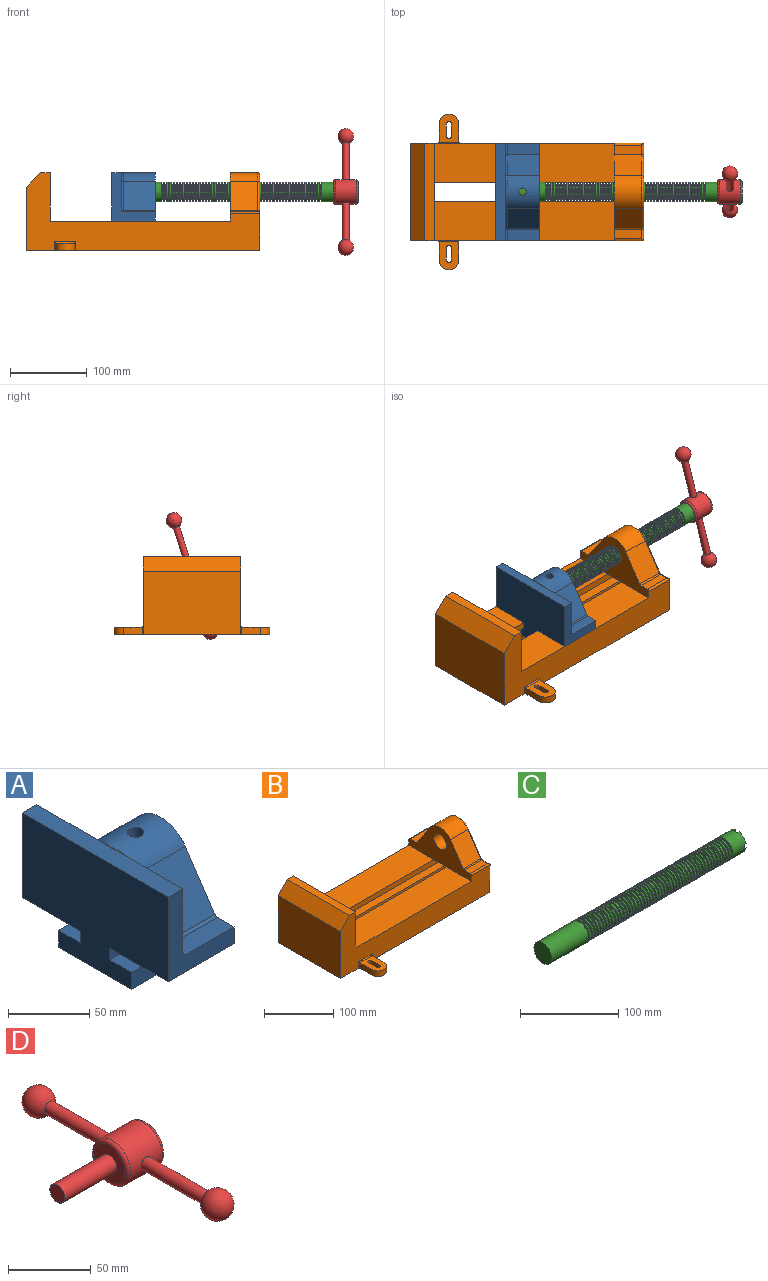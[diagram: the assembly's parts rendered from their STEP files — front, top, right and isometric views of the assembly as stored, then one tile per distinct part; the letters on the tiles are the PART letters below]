
ASSEMBLY  parts=4 mates=4
PART A: 36 faces, bbox 57.2x127x89 mm
  f0: plane 57.15x50.8mm, normal (0,0,-1), area 2903.2mm2, adj f6,f9,f10,f23
  f1: cylinder r=12.7mm len=44.45mm, axis (1,0,0), area 3464.3mm2, adj f6,f15,f16
  f2: plane 41.91x14.52mm, normal (0,0,1), area 608.5mm2, adj f6,f11,f24,f25
  f3: plane 51.86x48.26mm, normal (1,0,0), area 1495.7mm2, adj f8,f10,f31,f33,f35
  f4: plane 51.86x48.26mm, normal (1,0,0), area 1495.7mm2, adj f8,f11,f24,f28,f29
  f5: plane 57.15x50.8mm, normal (0,0,-1), area 2903.2mm2, adj f6,f9,f11,f22
  f6: plane 127x85.09mm, normal (1,0,0), area 5190.6mm2, adj f0,f1,f2,f5,f7,f10,f11,f12
  f7: plane 41.91x14.52mm, normal (0,0,1), area 608.5mm2, adj f6,f10,f30,f31
  f8: plane 127x12.7mm, normal (0,0,1), area 1612.9mm2, adj f3,f4,f9,f10,f11,f26,f34
  f9: plane 127x85.09mm, normal (-1,0,0), area 9096.8mm2, adj f0,f5,f8,f10,f11,f17,f18,f19
  f10: plane 63.5x57.15mm, normal (0,-1,0), area 1372.3mm2, adj f0,f3,f6,f7,f8,f9,f31
  f11: plane 63.5x57.15mm, normal (0,1,0), area 1372.3mm2, adj f2,f4,f5,f6,f8,f9,f24
  f12: plane 41.91x38.43mm, normal (0,-0.83,0.56), area 1939.2mm2, adj f6,f13,f30,f33
  f13: cylinder r=25.4mm len=44.45mm, axis (1,0,0), area 2026.5mm2, adj f6,f12,f14,f16,f26,f28,f34,f35
  f14: plane 41.91x38.43mm, normal (0,0.83,0.56), area 1939.2mm2, adj f6,f13,f25,f29
  f15: plane 25.4x25.4mm, normal (1,0,0), area 506.7mm2, adj f1
  f16: cylinder r=5.08mm len=13.76mm, axis (0,0,1), area 414mm2, adj f1,f13
  f17: plane 57.15x19.05mm, normal (0,0,1), area 1088.7mm2, adj f6,f9,f18,f23
  f18: plane 57.15x12.7mm, normal (0,-1,0), area 725.8mm2, adj f6,f9,f17,f19
  f19: plane 63.5x57.15mm, normal (0,0,-1), area 3629mm2, adj f6,f9,f18,f20
  f20: plane 57.15x12.7mm, normal (0,1,0), area 725.8mm2, adj f6,f9,f19,f21
  f21: plane 57.15x19.05mm, normal (0,0,1), area 1088.7mm2, adj f6,f9,f20,f22
  f22: plane 57.15x8.89mm, normal (0,1,0), area 508.1mm2, adj f5,f6,f9,f21
  f23: plane 57.15x8.89mm, normal (0,-1,0), area 508.1mm2, adj f0,f6,f9,f17
  f24: cylinder r=2.54mm len=14.52mm, axis (0,-1,0), area 57.9mm2, adj f2,f4,f11,f27
  f25: cylinder r=2.54mm len=41.91mm, axis (1,0,0), area 104.3mm2, adj f2,f6,f14,f27
  f26: bspline ~12.24x2.8mm, area 20.9mm2, adj f8,f13,f28
  f27: sphere r=2.54mm, area 6.3mm2, adj f24,f25,f29
  f28: torus R=27.94mm, axis (1,0,0), area 57.8mm2, adj f4,f13,f26,f29
  f29: cylinder r=2.54mm len=39.84mm, axis (0,-0.56,0.83), area 184.6mm2, adj f4,f14,f27,f28
  f30: cylinder r=2.54mm len=41.91mm, axis (1,0,0), area 104.3mm2, adj f6,f7,f12,f32
  f31: cylinder r=2.54mm len=14.52mm, axis (0,-1,0), area 57.9mm2, adj f3,f7,f10,f32
  f32: sphere r=2.54mm, area 6.3mm2, adj f30,f31,f33
  f33: cylinder r=2.54mm len=39.84mm, axis (0,-0.56,-0.83), area 184.6mm2, adj f3,f12,f32,f35
  f34: bspline ~12.24x2.8mm, area 20.9mm2, adj f8,f13,f35
  f35: torus R=27.94mm, axis (1,0,0), area 57.8mm2, adj f3,f13,f33,f34
PART B: 61 faces, bbox 304.8x203.2x103.7 mm
  f0: plane 304.8x101.6mm, normal (0,1,0), area 13520.3mm2, adj f3,f4,f5,f6,f7,f8,f9,f16
  f1: plane 304.8x101.6mm, normal (0,-1,0), area 13520.3mm2, adj f2,f3,f5,f6,f7,f8,f9,f16
  f2: plane 234.95x50.8mm, normal (0,0,1), area 11935.5mm2, adj f1,f5,f16,f26
  f3: plane 127x99.06mm, normal (1,0,0), area 7097.5mm2, adj f0,f1,f9,f14,f17,f18,f19,f20
  f4: plane 234.95x50.8mm, normal (0,0,1), area 11935.5mm2, adj f0,f5,f16,f27
  f5: plane 127x101.6mm, normal (1,0,0), area 9516.1mm2, adj f0,f1,f2,f4,f6,f9,f18,f19
  f6: plane 127x12.7mm, normal (0,0,1), area 1612.9mm2, adj f0,f1,f5,f7
  f7: plane 127x19.05mm, normal (-0.71,0,0.71), area 3421.5mm2, adj f0,f1,f6,f8
  f8: plane 127x82.55mm, normal (-1,0,0), area 10483.8mm2, adj f0,f1,f7,f9
  f9: plane 304.8x203.2mm, normal (0,0,-1), area 33298.3mm2, adj f0,f1,f3,f5,f8,f21,f22,f39
  f10: plane 35.56x11.98mm, normal (0,0,1), area 426mm2, adj f16,f28,f29,f30
  f11: plane 38.43x35.56mm, normal (0,0.83,0.56), area 1645.4mm2, adj f12,f16,f29,f32
  f12: cylinder r=25.4mm len=42.19mm, axis (1,0,0), area 1770.2mm2, adj f11,f13,f16,f33
  f13: plane 38.43x35.56mm, normal (0,-0.83,0.56), area 1645.4mm2, adj f12,f16,f34,f35
  f14: cylinder r=12.7mm len=38.1mm, axis (1,0,0), area 3040.2mm2, adj f3,f16
  f15: plane 35.56x11.98mm, normal (0,0,1), area 426mm2, adj f16,f34,f36,f38
  f16: plane 127x63.5mm, normal (-1,0,0), area 4155.5mm2, adj f0,f1,f2,f4,f10,f11,f12,f13
  f17: plane 38.1x25.4mm, normal (0,0,-1), area 967.7mm2, adj f3,f16,f26,f27
  f18: plane 273.05x19.05mm, normal (0,0,-1), area 5201.6mm2, adj f3,f5,f19,f26
  f19: plane 273.05x12.7mm, normal (0,1,0), area 3467.7mm2, adj f3,f5,f18,f20
  f20: plane 273.05x19.05mm, normal (0,0,1), area 5201.6mm2, adj f3,f5,f19,f21
  f21: plane 273.05x16.51mm, normal (0,1,0), area 4508.1mm2, adj f3,f5,f9,f20
  f22: plane 273.05x16.51mm, normal (0,-1,0), area 4508.1mm2, adj f3,f5,f9,f23
  f23: plane 273.05x19.05mm, normal (0,0,1), area 5201.6mm2, adj f3,f5,f22,f24
  f24: plane 273.05x12.7mm, normal (0,-1,0), area 3467.7mm2, adj f3,f5,f23,f25
  f25: plane 273.05x19.05mm, normal (0,0,-1), area 5201.6mm2, adj f3,f5,f24,f27
  f26: plane 273.05x8.89mm, normal (0,1,0), area 2427.4mm2, adj f2,f3,f5,f17,f18
  f27: plane 273.05x8.89mm, normal (0,-1,0), area 2427.4mm2, adj f3,f4,f5,f17,f25
  f28: cylinder r=2.54mm len=38.1mm, axis (1,0,0), area 148.3mm2, adj f0,f10,f16,f30
  f29: cylinder r=2.54mm len=35.56mm, axis (-1,0,0), area 88.5mm2, adj f10,f11,f16,f31
  f30: cylinder r=2.54mm len=14.52mm, axis (0,1,0), area 54.3mm2, adj f3,f10,f28,f31
  f31: torus R=5.08mm, axis (-1,0,0), area 13.5mm2, adj f3,f29,f30,f32
  f32: cylinder r=2.54mm len=39.84mm, axis (0,0.56,-0.83), area 184.6mm2, adj f3,f11,f31,f33
  f33: torus R=22.86mm, axis (-1,0,0), area 191.4mm2, adj f3,f12,f32,f35
  f34: cylinder r=2.54mm len=35.56mm, axis (-1,0,0), area 88.5mm2, adj f13,f15,f16,f37
  f35: cylinder r=2.54mm len=39.84mm, axis (0,0.56,0.83), area 184.6mm2, adj f3,f13,f33,f37
  f36: cylinder r=2.54mm len=38.1mm, axis (-1,0,0), area 148.3mm2, adj f1,f15,f16,f38
  f37: torus R=5.08mm, axis (-1,0,0), area 13.5mm2, adj f3,f34,f35,f38
  f38: cylinder r=2.54mm len=14.52mm, axis (0,1,0), area 54.3mm2, adj f3,f15,f36,f37
  f39: plane 23.88x9.53mm, normal (-1,0,0), area 227.4mm2, adj f9,f45,f46,f60
  f40: plane 23.88x9.53mm, normal (1,0,0), area 227.4mm2, adj f9,f45,f46,f58
  f41: cylinder r=3.3mm len=9.53mm, axis (0,0,-1), area 98.8mm2, adj f9,f42,f44,f46
  f42: plane 15.62x9.53mm, normal (-1,0,0), area 148.8mm2, adj f9,f41,f43,f46
  f43: cylinder r=3.3mm len=9.53mm, axis (0,0,-1), area 98.8mm2, adj f9,f42,f44,f46
  f44: plane 15.62x9.53mm, normal (1,0,0), area 148.8mm2, adj f9,f41,f43,f46
  f45: cylinder r=12.7mm len=25.4mm, axis (0,0,-1), area 380mm2, adj f9,f39,f40,f46
  f46: plane 36.58x25.4mm, normal (0,0,1), area 722.4mm2, adj f39,f40,f41,f42,f43,f44,f45,f59
  f47: plane 23.88x9.53mm, normal (-1,0,0), area 227.4mm2, adj f9,f53,f54,f56
  f48: plane 23.88x9.53mm, normal (1,0,0), area 227.4mm2, adj f9,f53,f54,f55
  f49: cylinder r=3.3mm len=9.53mm, axis (0,0,-1), area 98.8mm2, adj f9,f50,f52,f54
  f50: plane 15.62x9.53mm, normal (-1,0,0), area 148.8mm2, adj f9,f49,f51,f54
  f51: cylinder r=3.3mm len=9.53mm, axis (0,0,-1), area 98.8mm2, adj f9,f50,f52,f54
  f52: plane 15.62x9.53mm, normal (1,0,0), area 148.8mm2, adj f9,f49,f51,f54
  f53: cylinder r=12.7mm len=25.4mm, axis (0,0,-1), area 380mm2, adj f9,f47,f48,f54
  f54: plane 36.58x25.4mm, normal (0,0,1), area 722.4mm2, adj f47,f48,f49,f50,f51,f52,f53,f57
  f55: cylinder r=1.52mm len=11.05mm, axis (0,0,-1), area 24.1mm2, adj f0,f9,f48,f57
  f56: cylinder r=1.52mm len=11.05mm, axis (0,0,1), area 24.1mm2, adj f0,f9,f47,f57
  f57: cylinder r=1.52mm len=28.45mm, axis (1,0,0), area 63.5mm2, adj f0,f54,f55,f56
  f58: cylinder r=1.52mm len=11.05mm, axis (0,0,1), area 24.1mm2, adj f1,f9,f40,f59
  f59: cylinder r=1.52mm len=28.45mm, axis (-1,0,0), area 63.5mm2, adj f1,f46,f58,f60
  f60: cylinder r=1.52mm len=11.05mm, axis (0,0,-1), area 24.1mm2, adj f1,f9,f39,f59
PART C: 220 faces, bbox 279.4x25.4x25.4 mm
  f0: cylinder r=12.7mm len=25.4mm, axis (-1,0,0), area 1468.2mm2, adj f1,f2,f3,f5,f7,f208,f209,f210
  f1: plane 9.9x9.9mm, normal (1,0,0), area 62.3mm2, adj f0,f4,f213,f216
  f2: plane 9.9x9.9mm, normal (1,0,0), area 62.3mm2, adj f0,f4,f210,f218
  f3: plane 9.9x9.9mm, normal (1,0,0), area 62.3mm2, adj f0,f4,f209,f212
  f4: cylinder r=6.35mm len=25.4mm, axis (1,0,0), area 960.3mm2, adj f1,f2,f3,f5,f6,f208,f209,f210
  f5: plane 9.9x9.9mm, normal (1,0,0), area 62.3mm2, adj f0,f4,f215,f217
  f6: plane 12.7x12.7mm, normal (1,0,0), area 126.7mm2, adj f4
  f7: cone r=12.7mm half-angle=76deg, axis (1,0,0), area 188mm2, adj f0,f9
  f8: cone r=10.16mm half-angle=76deg, axis (-1,0,0), area 188mm2, adj f9,f10
  f9: cylinder r=10.16mm len=20.32mm, axis (1,0,0), area 81.1mm2, adj f7,f8
  f10: cylinder r=12.7mm len=25.4mm, axis (-1,0,0), area 131.7mm2, adj f8,f11
  f11: cone r=12.7mm half-angle=76deg, axis (1,0,0), area 188mm2, adj f10,f13
  f12: cone r=10.16mm half-angle=76deg, axis (-1,0,0), area 188mm2, adj f13,f14
  f13: cylinder r=10.16mm len=20.32mm, axis (1,0,0), area 81.1mm2, adj f11,f12
  f14: cylinder r=12.7mm len=25.4mm, axis (-1,0,0), area 131.7mm2, adj f12,f15
  f15: cone r=12.7mm half-angle=76deg, axis (1,0,0), area 188mm2, adj f14,f17
  f16: cone r=10.16mm half-angle=76deg, axis (-1,0,0), area 188mm2, adj f17,f18
  f17: cylinder r=10.16mm len=20.32mm, axis (1,0,0), area 81.1mm2, adj f15,f16
  f18: cylinder r=12.7mm len=25.4mm, axis (-1,0,0), area 131.7mm2, adj f16,f19
  f19: cone r=12.7mm half-angle=76deg, axis (1,0,0), area 188mm2, adj f18,f21
  f20: cone r=10.16mm half-angle=76deg, axis (-1,0,0), area 188mm2, adj f21,f22
  f21: cylinder r=10.16mm len=20.32mm, axis (1,0,0), area 81.1mm2, adj f19,f20
  f22: cylinder r=12.7mm len=25.4mm, axis (-1,0,0), area 131.7mm2, adj f20,f23
  f23: cone r=12.7mm half-angle=76deg, axis (1,0,0), area 188mm2, adj f22,f25
  f24: cone r=10.16mm half-angle=76deg, axis (-1,0,0), area 188mm2, adj f25,f26
  f25: cylinder r=10.16mm len=20.32mm, axis (1,0,0), area 81.1mm2, adj f23,f24
  f26: cylinder r=12.7mm len=25.4mm, axis (-1,0,0), area 131.7mm2, adj f24,f27
  f27: cone r=12.7mm half-angle=76deg, axis (1,0,0), area 188mm2, adj f26,f29
  f28: cone r=10.16mm half-angle=76deg, axis (-1,0,0), area 188mm2, adj f29,f30
  f29: cylinder r=10.16mm len=20.32mm, axis (1,0,0), area 81.1mm2, adj f27,f28
  f30: cylinder r=12.7mm len=25.4mm, axis (-1,0,0), area 131.7mm2, adj f28,f31
  f31: cone r=12.7mm half-angle=76deg, axis (1,0,0), area 188mm2, adj f30,f33
  f32: cone r=10.16mm half-angle=76deg, axis (-1,0,0), area 188mm2, adj f33,f34
  f33: cylinder r=10.16mm len=20.32mm, axis (1,0,0), area 81.1mm2, adj f31,f32
  f34: cylinder r=12.7mm len=25.4mm, axis (-1,0,0), area 131.7mm2, adj f32,f35
  f35: cone r=12.7mm half-angle=76deg, axis (1,0,0), area 188mm2, adj f34,f37
  f36: cone r=10.16mm half-angle=76deg, axis (-1,0,0), area 188mm2, adj f37,f38
  f37: cylinder r=10.16mm len=20.32mm, axis (1,0,0), area 81.1mm2, adj f35,f36
  f38: cylinder r=12.7mm len=25.4mm, axis (-1,0,0), area 131.7mm2, adj f36,f39
  f39: cone r=12.7mm half-angle=76deg, axis (1,0,0), area 188mm2, adj f38,f41
  f40: cone r=10.16mm half-angle=76deg, axis (-1,0,0), area 188mm2, adj f41,f42
  f41: cylinder r=10.16mm len=20.32mm, axis (1,0,0), area 81.1mm2, adj f39,f40
  f42: cylinder r=12.7mm len=25.4mm, axis (-1,0,0), area 131.7mm2, adj f40,f43
  f43: cone r=12.7mm half-angle=76deg, axis (1,0,0), area 188mm2, adj f42,f45
  f44: cone r=10.16mm half-angle=76deg, axis (-1,0,0), area 188mm2, adj f45,f46
  f45: cylinder r=10.16mm len=20.32mm, axis (1,0,0), area 81.1mm2, adj f43,f44
  f46: cylinder r=12.7mm len=25.4mm, axis (-1,0,0), area 131.7mm2, adj f44,f47
  f47: cone r=12.7mm half-angle=76deg, axis (1,0,0), area 188mm2, adj f46,f49
  f48: cone r=10.16mm half-angle=76deg, axis (-1,0,0), area 188mm2, adj f49,f50
  f49: cylinder r=10.16mm len=20.32mm, axis (1,0,0), area 81.1mm2, adj f47,f48
  f50: cylinder r=12.7mm len=25.4mm, axis (-1,0,0), area 131.7mm2, adj f48,f51
  f51: cone r=12.7mm half-angle=76deg, axis (1,0,0), area 188mm2, adj f50,f53
  f52: cone r=10.16mm half-angle=76deg, axis (-1,0,0), area 188mm2, adj f53,f54
  f53: cylinder r=10.16mm len=20.32mm, axis (1,0,0), area 81.1mm2, adj f51,f52
  f54: cylinder r=12.7mm len=25.4mm, axis (-1,0,0), area 131.7mm2, adj f52,f55
  f55: cone r=12.7mm half-angle=76deg, axis (1,0,0), area 188mm2, adj f54,f57
  f56: cone r=10.16mm half-angle=76deg, axis (-1,0,0), area 188mm2, adj f57,f58
  f57: cylinder r=10.16mm len=20.32mm, axis (1,0,0), area 81.1mm2, adj f55,f56
  f58: cylinder r=12.7mm len=25.4mm, axis (-1,0,0), area 131.7mm2, adj f56,f59
  f59: cone r=12.7mm half-angle=76deg, axis (1,0,0), area 188mm2, adj f58,f61
  f60: cone r=10.16mm half-angle=76deg, axis (-1,0,0), area 188mm2, adj f61,f62
  f61: cylinder r=10.16mm len=20.32mm, axis (1,0,0), area 81.1mm2, adj f59,f60
  f62: cylinder r=12.7mm len=25.4mm, axis (-1,0,0), area 131.7mm2, adj f60,f63
  f63: cone r=12.7mm half-angle=76deg, axis (1,0,0), area 188mm2, adj f62,f65
  f64: cone r=10.16mm half-angle=76deg, axis (-1,0,0), area 188mm2, adj f65,f66
  f65: cylinder r=10.16mm len=20.32mm, axis (1,0,0), area 81.1mm2, adj f63,f64
  f66: cylinder r=12.7mm len=25.4mm, axis (-1,0,0), area 131.7mm2, adj f64,f67
  f67: cone r=12.7mm half-angle=76deg, axis (1,0,0), area 188mm2, adj f66,f69
  f68: cone r=10.16mm half-angle=76deg, axis (-1,0,0), area 188mm2, adj f69,f70
  f69: cylinder r=10.16mm len=20.32mm, axis (1,0,0), area 81.1mm2, adj f67,f68
  f70: cylinder r=12.7mm len=25.4mm, axis (-1,0,0), area 131.7mm2, adj f68,f71
  f71: cone r=12.7mm half-angle=76deg, axis (1,0,0), area 188mm2, adj f70,f73
  f72: cone r=10.16mm half-angle=76deg, axis (-1,0,0), area 188mm2, adj f73,f74
  f73: cylinder r=10.16mm len=20.32mm, axis (1,0,0), area 81.1mm2, adj f71,f72
  f74: cylinder r=12.7mm len=25.4mm, axis (-1,0,0), area 131.7mm2, adj f72,f75
  f75: cone r=12.7mm half-angle=76deg, axis (1,0,0), area 188mm2, adj f74,f77
  f76: cone r=10.16mm half-angle=76deg, axis (-1,0,0), area 188mm2, adj f77,f78
  f77: cylinder r=10.16mm len=20.32mm, axis (1,0,0), area 81.1mm2, adj f75,f76
  f78: cylinder r=12.7mm len=25.4mm, axis (-1,0,0), area 131.7mm2, adj f76,f79
  f79: cone r=12.7mm half-angle=76deg, axis (1,0,0), area 188mm2, adj f78,f81
  f80: cone r=10.16mm half-angle=76deg, axis (-1,0,0), area 188mm2, adj f81,f82
  f81: cylinder r=10.16mm len=20.32mm, axis (1,0,0), area 81.1mm2, adj f79,f80
  f82: cylinder r=12.7mm len=25.4mm, axis (-1,0,0), area 131.7mm2, adj f80,f83
  f83: cone r=12.7mm half-angle=76deg, axis (1,0,0), area 188mm2, adj f82,f85
  f84: cone r=10.16mm half-angle=76deg, axis (-1,0,0), area 188mm2, adj f85,f86
  f85: cylinder r=10.16mm len=20.32mm, axis (1,0,0), area 81.1mm2, adj f83,f84
  f86: cylinder r=12.7mm len=25.4mm, axis (-1,0,0), area 131.7mm2, adj f84,f87
  f87: cone r=12.7mm half-angle=76deg, axis (1,0,0), area 188mm2, adj f86,f89
  f88: cone r=10.16mm half-angle=76deg, axis (-1,0,0), area 188mm2, adj f89,f90
  f89: cylinder r=10.16mm len=20.32mm, axis (1,0,0), area 81.1mm2, adj f87,f88
  f90: cylinder r=12.7mm len=25.4mm, axis (-1,0,0), area 131.7mm2, adj f88,f91
  f91: cone r=12.7mm half-angle=76deg, axis (1,0,0), area 188mm2, adj f90,f93
  f92: cone r=10.16mm half-angle=76deg, axis (-1,0,0), area 188mm2, adj f93,f94
  f93: cylinder r=10.16mm len=20.32mm, axis (1,0,0), area 81.1mm2, adj f91,f92
  f94: cylinder r=12.7mm len=25.4mm, axis (-1,0,0), area 131.7mm2, adj f92,f95
  f95: cone r=12.7mm half-angle=76deg, axis (1,0,0), area 188mm2, adj f94,f97
  f96: cone r=10.16mm half-angle=76deg, axis (-1,0,0), area 188mm2, adj f97,f98
  f97: cylinder r=10.16mm len=20.32mm, axis (1,0,0), area 81.1mm2, adj f95,f96
  f98: cylinder r=12.7mm len=25.4mm, axis (-1,0,0), area 131.7mm2, adj f96,f99
  f99: cone r=12.7mm half-angle=76deg, axis (1,0,0), area 188mm2, adj f98,f101
  f100: cone r=10.16mm half-angle=76deg, axis (-1,0,0), area 188mm2, adj f101,f102
  f101: cylinder r=10.16mm len=20.32mm, axis (1,0,0), area 81.1mm2, adj f99,f100
  f102: cylinder r=12.7mm len=25.4mm, axis (-1,0,0), area 131.7mm2, adj f100,f103
  f103: cone r=12.7mm half-angle=76deg, axis (1,0,0), area 188mm2, adj f102,f105
  f104: cone r=10.16mm half-angle=76deg, axis (-1,0,0), area 188mm2, adj f105,f106
  f105: cylinder r=10.16mm len=20.32mm, axis (1,0,0), area 81.1mm2, adj f103,f104
  f106: cylinder r=12.7mm len=25.4mm, axis (-1,0,0), area 131.7mm2, adj f104,f107
  f107: cone r=12.7mm half-angle=76deg, axis (1,0,0), area 188mm2, adj f106,f109
  f108: cone r=10.16mm half-angle=76deg, axis (-1,0,0), area 188mm2, adj f109,f110
  f109: cylinder r=10.16mm len=20.32mm, axis (1,0,0), area 81.1mm2, adj f107,f108
  f110: cylinder r=12.7mm len=25.4mm, axis (-1,0,0), area 131.7mm2, adj f108,f111
  f111: cone r=12.7mm half-angle=76deg, axis (1,0,0), area 188mm2, adj f110,f113
  f112: cone r=10.16mm half-angle=76deg, axis (-1,0,0), area 188mm2, adj f113,f114
  f113: cylinder r=10.16mm len=20.32mm, axis (1,0,0), area 81.1mm2, adj f111,f112
  f114: cylinder r=12.7mm len=25.4mm, axis (-1,0,0), area 131.7mm2, adj f112,f115
  f115: cone r=12.7mm half-angle=76deg, axis (1,0,0), area 188mm2, adj f114,f117
  f116: cone r=10.16mm half-angle=76deg, axis (-1,0,0), area 188mm2, adj f117,f118
  f117: cylinder r=10.16mm len=20.32mm, axis (1,0,0), area 81.1mm2, adj f115,f116
  f118: cylinder r=12.7mm len=25.4mm, axis (-1,0,0), area 131.7mm2, adj f116,f119
  f119: cone r=12.7mm half-angle=76deg, axis (1,0,0), area 188mm2, adj f118,f121
  f120: cone r=10.16mm half-angle=76deg, axis (-1,0,0), area 188mm2, adj f121,f122
  f121: cylinder r=10.16mm len=20.32mm, axis (1,0,0), area 81.1mm2, adj f119,f120
  f122: cylinder r=12.7mm len=25.4mm, axis (-1,0,0), area 131.7mm2, adj f120,f123
  f123: cone r=12.7mm half-angle=76deg, axis (1,0,0), area 188mm2, adj f122,f125
  f124: cone r=10.16mm half-angle=76deg, axis (-1,0,0), area 188mm2, adj f125,f126
  f125: cylinder r=10.16mm len=20.32mm, axis (1,0,0), area 81.1mm2, adj f123,f124
  f126: cylinder r=12.7mm len=25.4mm, axis (-1,0,0), area 131.7mm2, adj f124,f127
  f127: cone r=12.7mm half-angle=76deg, axis (1,0,0), area 188mm2, adj f126,f129
  f128: cone r=10.16mm half-angle=76deg, axis (-1,0,0), area 188mm2, adj f129,f130
  f129: cylinder r=10.16mm len=20.32mm, axis (1,0,0), area 81.1mm2, adj f127,f128
  f130: cylinder r=12.7mm len=25.4mm, axis (-1,0,0), area 131.7mm2, adj f128,f131
  f131: cone r=12.7mm half-angle=76deg, axis (1,0,0), area 188mm2, adj f130,f133
  f132: cone r=10.16mm half-angle=76deg, axis (-1,0,0), area 188mm2, adj f133,f134
  f133: cylinder r=10.16mm len=20.32mm, axis (1,0,0), area 81.1mm2, adj f131,f132
  f134: cylinder r=12.7mm len=25.4mm, axis (-1,0,0), area 131.7mm2, adj f132,f135
  f135: cone r=12.7mm half-angle=76deg, axis (1,0,0), area 188mm2, adj f134,f137
  f136: cone r=10.16mm half-angle=76deg, axis (-1,0,0), area 188mm2, adj f137,f138
  f137: cylinder r=10.16mm len=20.32mm, axis (1,0,0), area 81.1mm2, adj f135,f136
  f138: cylinder r=12.7mm len=25.4mm, axis (-1,0,0), area 131.7mm2, adj f136,f139
  f139: cone r=12.7mm half-angle=76deg, axis (1,0,0), area 188mm2, adj f138,f141
  f140: cone r=10.16mm half-angle=76deg, axis (-1,0,0), area 188mm2, adj f141,f142
  f141: cylinder r=10.16mm len=20.32mm, axis (1,0,0), area 81.1mm2, adj f139,f140
  f142: cylinder r=12.7mm len=25.4mm, axis (-1,0,0), area 131.7mm2, adj f140,f143
  f143: cone r=12.7mm half-angle=76deg, axis (1,0,0), area 188mm2, adj f142,f145
  f144: cone r=10.16mm half-angle=76deg, axis (-1,0,0), area 188mm2, adj f145,f146
  f145: cylinder r=10.16mm len=20.32mm, axis (1,0,0), area 81.1mm2, adj f143,f144
  f146: cylinder r=12.7mm len=25.4mm, axis (-1,0,0), area 131.7mm2, adj f144,f147
  f147: cone r=12.7mm half-angle=76deg, axis (1,0,0), area 188mm2, adj f146,f149
  f148: cone r=10.16mm half-angle=76deg, axis (-1,0,0), area 188mm2, adj f149,f150
  f149: cylinder r=10.16mm len=20.32mm, axis (1,0,0), area 81.1mm2, adj f147,f148
  f150: cylinder r=12.7mm len=25.4mm, axis (-1,0,0), area 131.7mm2, adj f148,f151
  f151: cone r=12.7mm half-angle=76deg, axis (1,0,0), area 188mm2, adj f150,f153
  f152: cone r=10.16mm half-angle=76deg, axis (-1,0,0), area 188mm2, adj f153,f154
  f153: cylinder r=10.16mm len=20.32mm, axis (1,0,0), area 81.1mm2, adj f151,f152
  f154: cylinder r=12.7mm len=25.4mm, axis (-1,0,0), area 131.7mm2, adj f152,f155
  f155: cone r=12.7mm half-angle=76deg, axis (1,0,0), area 188mm2, adj f154,f157
  f156: cone r=10.16mm half-angle=76deg, axis (-1,0,0), area 188mm2, adj f157,f158
  f157: cylinder r=10.16mm len=20.32mm, axis (1,0,0), area 81.1mm2, adj f155,f156
  f158: cylinder r=12.7mm len=25.4mm, axis (-1,0,0), area 131.7mm2, adj f156,f159
  f159: cone r=12.7mm half-angle=76deg, axis (1,0,0), area 188mm2, adj f158,f161
  f160: cone r=10.16mm half-angle=76deg, axis (-1,0,0), area 188mm2, adj f161,f162
  f161: cylinder r=10.16mm len=20.32mm, axis (1,0,0), area 81.1mm2, adj f159,f160
  f162: cylinder r=12.7mm len=25.4mm, axis (-1,0,0), area 131.7mm2, adj f160,f163
  f163: cone r=12.7mm half-angle=76deg, axis (1,0,0), area 188mm2, adj f162,f165
  f164: cone r=10.16mm half-angle=76deg, axis (-1,0,0), area 188mm2, adj f165,f166
  f165: cylinder r=10.16mm len=20.32mm, axis (1,0,0), area 81.1mm2, adj f163,f164
  f166: cylinder r=12.7mm len=25.4mm, axis (-1,0,0), area 131.7mm2, adj f164,f167
  f167: cone r=12.7mm half-angle=76deg, axis (1,0,0), area 188mm2, adj f166,f169
  f168: cone r=10.16mm half-angle=76deg, axis (-1,0,0), area 188mm2, adj f169,f170
  f169: cylinder r=10.16mm len=20.32mm, axis (1,0,0), area 81.1mm2, adj f167,f168
  f170: cylinder r=12.7mm len=25.4mm, axis (-1,0,0), area 131.7mm2, adj f168,f171
  f171: cone r=12.7mm half-angle=76deg, axis (1,0,0), area 188mm2, adj f170,f173
  f172: cone r=10.16mm half-angle=76deg, axis (-1,0,0), area 188mm2, adj f173,f174
  f173: cylinder r=10.16mm len=20.32mm, axis (1,0,0), area 81.1mm2, adj f171,f172
  f174: cylinder r=12.7mm len=25.4mm, axis (-1,0,0), area 131.7mm2, adj f172,f175
  f175: cone r=12.7mm half-angle=76deg, axis (1,0,0), area 188mm2, adj f174,f177
  f176: cone r=10.16mm half-angle=76deg, axis (-1,0,0), area 188mm2, adj f177,f178
  f177: cylinder r=10.16mm len=20.32mm, axis (1,0,0), area 81.1mm2, adj f175,f176
  f178: cylinder r=12.7mm len=25.4mm, axis (-1,0,0), area 131.7mm2, adj f176,f179
  f179: cone r=12.7mm half-angle=76deg, axis (1,0,0), area 188mm2, adj f178,f181
  f180: cone r=10.16mm half-angle=76deg, axis (-1,0,0), area 188mm2, adj f181,f182
  f181: cylinder r=10.16mm len=20.32mm, axis (1,0,0), area 81.1mm2, adj f179,f180
  f182: cylinder r=12.7mm len=25.4mm, axis (-1,0,0), area 131.7mm2, adj f180,f183
  f183: cone r=12.7mm half-angle=76deg, axis (1,0,0), area 188mm2, adj f182,f185
  f184: cone r=10.16mm half-angle=76deg, axis (-1,0,0), area 188mm2, adj f185,f186
  f185: cylinder r=10.16mm len=20.32mm, axis (1,0,0), area 81.1mm2, adj f183,f184
  f186: cylinder r=12.7mm len=25.4mm, axis (-1,0,0), area 131.7mm2, adj f184,f187
  f187: cone r=12.7mm half-angle=76deg, axis (1,0,0), area 188mm2, adj f186,f189
  f188: cone r=10.16mm half-angle=76deg, axis (-1,0,0), area 188mm2, adj f189,f190
  f189: cylinder r=10.16mm len=20.32mm, axis (1,0,0), area 81.1mm2, adj f187,f188
  f190: cylinder r=12.7mm len=25.4mm, axis (-1,0,0), area 131.7mm2, adj f188,f191
  f191: cone r=12.7mm half-angle=76deg, axis (1,0,0), area 188mm2, adj f190,f193
  f192: cone r=10.16mm half-angle=76deg, axis (-1,0,0), area 188mm2, adj f193,f194
  f193: cylinder r=10.16mm len=20.32mm, axis (1,0,0), area 81.1mm2, adj f191,f192
  f194: cylinder r=12.7mm len=25.4mm, axis (-1,0,0), area 131.7mm2, adj f192,f195
  f195: cone r=12.7mm half-angle=76deg, axis (1,0,0), area 188mm2, adj f194,f197
  f196: cone r=10.16mm half-angle=76deg, axis (-1,0,0), area 188mm2, adj f197,f198
  f197: cylinder r=10.16mm len=20.32mm, axis (1,0,0), area 81.1mm2, adj f195,f196
  f198: cylinder r=12.7mm len=25.4mm, axis (-1,0,0), area 131.7mm2, adj f196,f199
  f199: cone r=12.7mm half-angle=76deg, axis (1,0,0), area 188mm2, adj f198,f201
  f200: cone r=10.16mm half-angle=76deg, axis (-1,0,0), area 188mm2, adj f201,f202
  f201: cylinder r=10.16mm len=20.32mm, axis (1,0,0), area 81.1mm2, adj f199,f200
  f202: cylinder r=12.7mm len=25.4mm, axis (-1,0,0), area 131.7mm2, adj f200,f203
  f203: cone r=12.7mm half-angle=76deg, axis (1,0,0), area 188mm2, adj f202,f205
  f204: cone r=10.16mm half-angle=76deg, axis (-1,0,0), area 188mm2, adj f205,f207
  f205: cylinder r=10.16mm len=20.32mm, axis (1,0,0), area 81.1mm2, adj f203,f204
  f206: plane 25.4x25.4mm, normal (-1,0,0), area 506.7mm2, adj f207
  f207: cylinder r=12.7mm len=52.45mm, axis (-1,0,0), area 4185.4mm2, adj f204,f206
  f208: plane 6.88x5.08mm, normal (1,0,0), area 32.7mm2, adj f0,f4,f209,f210
  f209: plane 6.62x2.54mm, normal (0,-1,0), area 16.8mm2, adj f0,f3,f4,f208
  f210: plane 6.62x2.54mm, normal (0,1,0), area 16.8mm2, adj f0,f2,f4,f208
  f211: plane 6.88x5.08mm, normal (1,0,0), area 32.7mm2, adj f0,f4,f212,f213
  f212: plane 6.62x2.54mm, normal (0,0,1), area 16.8mm2, adj f0,f3,f4,f211
  f213: plane 6.62x2.54mm, normal (0,0,-1), area 16.8mm2, adj f0,f1,f4,f211
  f214: plane 6.88x5.08mm, normal (1,0,0), area 32.7mm2, adj f0,f4,f215,f216
  f215: plane 6.62x2.54mm, normal (0,1,0), area 16.8mm2, adj f0,f4,f5,f214
  f216: plane 6.62x2.54mm, normal (0,-1,0), area 16.8mm2, adj f0,f1,f4,f214
  f217: plane 6.62x2.54mm, normal (0,0,-1), area 16.8mm2, adj f0,f4,f5,f219
  f218: plane 6.62x2.54mm, normal (0,0,1), area 16.8mm2, adj f0,f2,f4,f219
  f219: plane 6.88x5.08mm, normal (1,0,0), area 32.7mm2, adj f0,f4,f217,f218
PART D: 11 faces, bbox 76.2x172.7x34.4 mm
  f0: sphere r=10.16mm, area 1231.8mm2, adj f1
  f1: cylinder r=4.45mm len=51.82mm, axis (0,1,0), area 1438.5mm2, adj f0,f4
  f2: sphere r=10.16mm, area 1231.8mm2, adj f3
  f3: cylinder r=4.45mm len=51.82mm, axis (0,1,0), area 1438.5mm2, adj f2,f4
  f4: cylinder r=15.88mm len=31.75mm, axis (-1,0,0), area 2534.7mm2, adj f1,f3,f9,f10
  f5: cylinder r=6.35mm len=44.45mm, axis (-1,0,0), area 1773.5mm2, adj f6,f8
  f6: plane 12.7x12.7mm, normal (-1,0,0), area 126.7mm2, adj f5
  f7: plane 26.67x26.67mm, normal (1,0,0), area 558.6mm2, adj f10
  f8: plane 26.67x26.67mm, normal (-1,0,0), area 432mm2, adj f5,f9
  f9: torus R=13.33mm, axis (1,0,0), area 374.8mm2, adj f4,f8
  f10: torus R=13.33mm, axis (1,0,0), area 374.8mm2, adj f4,f7
PLACE A t=(80.01,0,0)mm
PLACE B at identity fixed
PLACE C rot(axis=(1,0,0),72deg) t=(80.01,72.47,52.65)mm
PLACE D rot(axis=(1,0,0),72deg) t=(58.42,72.47,52.65)mm
MATE planar A.f0 <-> B.f2  axis (0,0,-1) through (-164.47,-38.1,38.1)mm
MATE cylindrical B.f12 <-> C.f7  axis (-1,0,0) through (-38.1,0,76.2)mm
MATE revolute C.f7 <-> A.f28  axis (-1,0,0) through (-180.34,0,76.2)mm
MATE fastened C.f4 <-> D.f5  axis (1,0,0) through (96.52,0,76.2)mm
